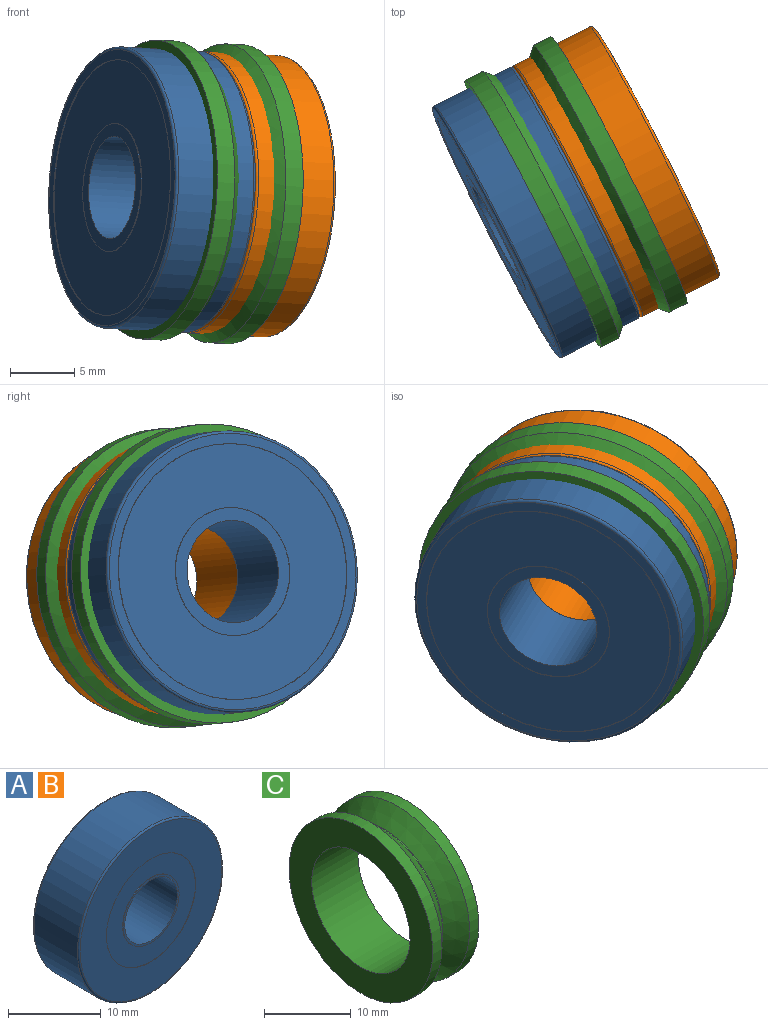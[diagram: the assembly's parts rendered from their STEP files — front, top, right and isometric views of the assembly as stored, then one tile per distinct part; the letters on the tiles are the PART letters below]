
ASSEMBLY  parts=3 mates=2
PART A: 14 faces, bbox 23.8x7x23.8 mm
  f0: plane 8.53x8.53mm, normal (0,-1,0), area 6.9mm2, adj f2,f9
  f1: plane 10.01x10.01mm, normal (0,1,0), area 28.4mm2, adj f2,f6
  f2: cylinder r=4mm len=8mm, axis (0,1,0), area 176.2mm2, adj f0,f1
  f3: cylinder r=11mm len=22mm, axis (0,1,0), area 456.4mm2, adj f12,f13
  f4: plane 21.59x21.59mm, normal (0,-1,0), area 221.6mm2, adj f10,f13
  f5: plane 21.59x21.59mm, normal (0,1,0), area 52.3mm2, adj f7,f12
  f6: cylinder r=5mm len=10.01mm, axis (0,1,0), area 1.6mm2, adj f1,f8
  f7: cylinder r=9.99mm len=19.99mm, axis (0,1,0), area 3.2mm2, adj f5,f8
  f8: plane 19.99x19.99mm, normal (0,1,0), area 235.2mm2, adj f6,f7
  f9: cylinder r=4.27mm len=8.53mm, axis (0,-1,0), area 1.4mm2, adj f0,f11
  f10: cylinder r=6.78mm len=13.56mm, axis (0,-1,0), area 2.2mm2, adj f4,f11
  f11: plane 13.56x13.56mm, normal (0,-1,0), area 87.3mm2, adj f9,f10
  f12: torus R=10.79mm, axis (0,-1,0), area 21.9mm2, adj f3,f5
  f13: torus R=10.79mm, axis (0,-1,0), area 21.9mm2, adj f3,f4
PART B: same geometry as A
PART C: 8 faces, bbox 7.5x23.4x23.4 mm
  f0: cylinder r=9.53mm len=19.05mm, axis (-1,0,0), area 9.1mm2, adj f1,f7
  f1: cone r=9.53mm half-angle=45deg, axis (-1,0,0), area 203.4mm2, adj f0,f2
  f2: cylinder r=11.68mm len=23.37mm, axis (-1,0,0), area 111.9mm2, adj f1,f3
  f3: plane 23.37x23.37mm, normal (-1,0,0), area 227.8mm2, adj f2,f4
  f4: cylinder r=8mm len=16mm, axis (-1,0,0), area 378mm2, adj f3,f5
  f5: plane 23.37x23.37mm, normal (1,0,0), area 227.8mm2, adj f4,f6
  f6: cylinder r=11.68mm len=23.37mm, axis (-1,0,0), area 111.9mm2, adj f5,f7
  f7: cone r=9.53mm half-angle=45deg, axis (1,0,0), area 203.4mm2, adj f0,f6
PLACE A rot(axis=(-0.69,0.44,0.58),143.5deg) t=(-28.55,-26.06,-114.51)mm
PLACE B rot(axis=(-0.14,-0.14,-0.98),63.7deg) t=(-16.07,-19.7,-115.2)mm
PLACE C rot(axis=(-0.41,0,0.91),29.8deg) t=(-22.31,-22.88,-114.86)mm
MATE revolute A.f9 <-> C.f0  axis (0.89,0.45,-0.05) through (-22.31,-22.88,-114.86)mm
MATE revolute B.f9 <-> A.f9  axis (-0.89,-0.45,0.05) through (-22.31,-22.88,-114.86)mm
